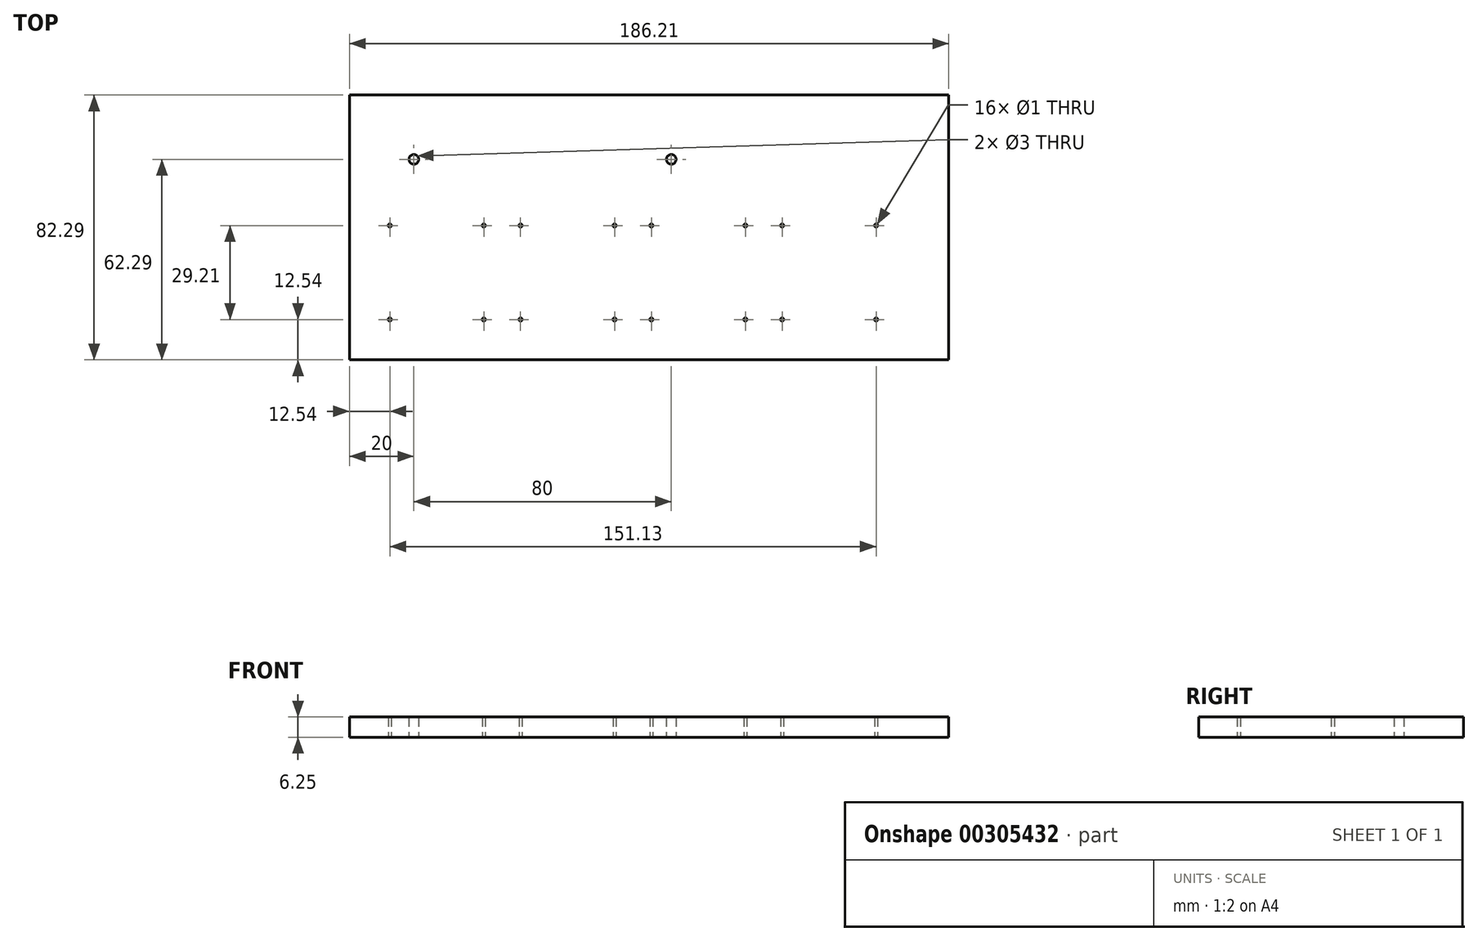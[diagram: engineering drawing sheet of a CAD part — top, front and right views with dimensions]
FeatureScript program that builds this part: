
annotation { "Feature Type Name" : "Feature", "Feature Type Description" : "" }
export const myFeature = defineFeature(function(context is Context, id is Id, definition is map)
    precondition{}
    {
        {
            var Q0;
            Q0=qCreatedBy(makeId("Top.planeOp"),FACE);
            var sketch = newSketch(context, id + "F0", { "sketchPlane" : qUnion([Q0])});
            skLineSegment(sketch, "E0.bottom", {"start": v(0, 0) * mm, "end": v(34.3, 0) * mm, "construction": true});
            skLineSegment(sketch, "E0.top", {"start": v(0, 34.3) * mm, "end": v(34.3, 34.3) * mm, "construction": true});
            skLineSegment(sketch, "E0.left", {"start": v(0, 0) * mm, "end": v(0, 34.3) * mm, "construction": true});
            skLineSegment(sketch, "E0.right", {"start": v(34.29, 0) * mm, "end": v(34.29, 34.3) * mm, "construction": true});
            skLineSegment(sketch, "E1.bottom", {"start": v(2.54, 31.75) * mm, "end": v(31.75, 31.75) * mm, "construction": true});
            skLineSegment(sketch, "E1.top", {"start": v(2.54, 2.54) * mm, "end": v(31.75, 2.54) * mm, "construction": true});
            skLineSegment(sketch, "E1.left", {"start": v(2.54, 31.75) * mm, "end": v(2.54, 2.54) * mm, "construction": true});
            skLineSegment(sketch, "E1.right", {"start": v(31.75, 31.75) * mm, "end": v(31.75, 2.54) * mm, "construction": true});
            skPoint(sketch, "E2", {"position": v(17.15, 31.75) * mm});
            skPoint(sketch, "E3", {"position": v(17.15, 34.3) * mm});
            skPoint(sketch, "E4", {"position": v(34.29, 17.15) * mm});
            skPoint(sketch, "E5", {"position": v(31.75, 17.15) * mm});
            skLineSegment(sketch, "E6.1.0.0", {"start": v(40.64, 0) * mm, "end": v(40.64, 34.3) * mm, "construction": true});
            skPoint(sketch, "E6.1.0.1", {"position": v(72.39, 17.15) * mm});
            skLineSegment(sketch, "E6.1.0.2", {"start": v(74.93, 0) * mm, "end": v(74.93, 34.3) * mm, "construction": true});
            skPoint(sketch, "E6.1.0.3", {"position": v(74.93, 17.15) * mm});
            skLineSegment(sketch, "E6.1.0.4", {"start": v(43.18, 31.75) * mm, "end": v(72.39, 31.75) * mm, "construction": true});
            skPoint(sketch, "E6.1.0.5", {"position": v(57.78, 34.3) * mm});
            skLineSegment(sketch, "E6.1.0.6", {"start": v(43.18, 2.54) * mm, "end": v(72.39, 2.54) * mm, "construction": true});
            skLineSegment(sketch, "E6.1.0.7", {"start": v(40.64, 34.3) * mm, "end": v(74.93, 34.3) * mm, "construction": true});
            skLineSegment(sketch, "E6.1.0.8", {"start": v(43.18, 31.75) * mm, "end": v(43.18, 2.54) * mm, "construction": true});
            skPoint(sketch, "E6.1.0.9", {"position": v(57.78, 31.75) * mm});
            skLineSegment(sketch, "E6.1.0.10", {"start": v(72.39, 31.75) * mm, "end": v(72.39, 2.54) * mm, "construction": true});
            skLineSegment(sketch, "E6.1.0.11", {"start": v(40.64, 0) * mm, "end": v(74.93, 0) * mm, "construction": true});
            skLineSegment(sketch, "E6.2.0.0", {"start": v(81.28, 0) * mm, "end": v(81.28, 34.3) * mm, "construction": true});
            skPoint(sketch, "E6.2.0.1", {"position": v(113.03, 17.15) * mm});
            skLineSegment(sketch, "E6.2.0.2", {"start": v(115.57, 0) * mm, "end": v(115.57, 34.3) * mm, "construction": true});
            skPoint(sketch, "E6.2.0.3", {"position": v(115.57, 17.15) * mm});
            skLineSegment(sketch, "E6.2.0.4", {"start": v(83.82, 31.75) * mm, "end": v(113.03, 31.75) * mm, "construction": true});
            skPoint(sketch, "E6.2.0.5", {"position": v(98.42, 34.3) * mm});
            skLineSegment(sketch, "E6.2.0.6", {"start": v(83.82, 2.54) * mm, "end": v(113.03, 2.54) * mm, "construction": true});
            skLineSegment(sketch, "E6.2.0.7", {"start": v(81.28, 34.3) * mm, "end": v(115.57, 34.3) * mm, "construction": true});
            skLineSegment(sketch, "E6.2.0.8", {"start": v(83.82, 31.75) * mm, "end": v(83.82, 2.54) * mm, "construction": true});
            skPoint(sketch, "E6.2.0.9", {"position": v(98.42, 31.75) * mm});
            skLineSegment(sketch, "E6.2.0.10", {"start": v(113.03, 31.75) * mm, "end": v(113.03, 2.54) * mm, "construction": true});
            skLineSegment(sketch, "E6.2.0.11", {"start": v(81.28, 0) * mm, "end": v(115.57, 0) * mm, "construction": true});
            skLineSegment(sketch, "E6.3.0.0", {"start": v(121.92, 0) * mm, "end": v(121.92, 34.3) * mm, "construction": true});
            skPoint(sketch, "E6.3.0.1", {"position": v(153.67, 17.15) * mm});
            skLineSegment(sketch, "E6.3.0.2", {"start": v(156.2, 0) * mm, "end": v(156.2, 34.3) * mm, "construction": true});
            skPoint(sketch, "E6.3.0.3", {"position": v(156.2, 17.15) * mm});
            skLineSegment(sketch, "E6.3.0.4", {"start": v(124.46, 31.75) * mm, "end": v(153.67, 31.75) * mm, "construction": true});
            skPoint(sketch, "E6.3.0.5", {"position": v(139.06, 34.3) * mm});
            skLineSegment(sketch, "E6.3.0.6", {"start": v(124.46, 2.54) * mm, "end": v(153.67, 2.54) * mm, "construction": true});
            skLineSegment(sketch, "E6.3.0.7", {"start": v(121.92, 34.3) * mm, "end": v(156.2, 34.3) * mm, "construction": true});
            skLineSegment(sketch, "E6.3.0.8", {"start": v(124.46, 31.75) * mm, "end": v(124.46, 2.54) * mm, "construction": true});
            skPoint(sketch, "E6.3.0.9", {"position": v(139.06, 31.75) * mm});
            skLineSegment(sketch, "E6.3.0.10", {"start": v(153.67, 31.75) * mm, "end": v(153.67, 2.54) * mm, "construction": true});
            skLineSegment(sketch, "E6.3.0.11", {"start": v(121.92, 0) * mm, "end": v(156.2, 0) * mm, "construction": true});
            skLineSegment(sketch, "E6.direction1", {"start": v(0, 0) * mm, "end": v(40.64, 0) * mm, "construction": true});
            skLineSegment(sketch, "E7.bottom", {"start": v(0, 62.3) * mm, "end": v(100, 62.3) * mm, "construction": true});
            skLineSegment(sketch, "E7.top", {"start": v(0, 42.3) * mm, "end": v(100, 42.29) * mm, "construction": true});
            skLineSegment(sketch, "E7.left", {"start": v(0, 62.29) * mm, "end": v(0, 42.3) * mm, "construction": true});
            skLineSegment(sketch, "E7.right", {"start": v(100, 62.29) * mm, "end": v(100, 42.3) * mm, "construction": true});
            skPoint(sketch, "E8", {"position": v(0, 52.29) * mm});
            skPoint(sketch, "E9", {"position": v(10, 52.29) * mm});
            skPoint(sketch, "E10", {"position": v(90, 52.3) * mm});
            skPoint(sketch, "E11", {"position": v(50, 62.3) * mm});
            skPoint(sketch, "E12", {"position": v(50, 52.29) * mm});
            skPoint(sketch, "E13.endSnap0", {"position": v(50, 42.3) * mm});
            skLineSegment(sketch, "E14.bottom", {"start": v(-10, -10) * mm, "end": v(176.2, -10) * mm});
            skLineSegment(sketch, "E14.top", {"start": v(-10, 72.29) * mm, "end": v(176.2, 72.29) * mm});
            skLineSegment(sketch, "E14.left", {"start": v(-10, -10) * mm, "end": v(-10, 72.29) * mm});
            skLineSegment(sketch, "E14.right", {"start": v(176.2, -10) * mm, "end": v(176.2, 72.29) * mm});
            skSolve(sketch);
        }
        {
            var Q0;
            Q0=makeQuery(id+"F0.imprint","IMPRINT",FACE,{"disambiguationData":[TD([[makeQuery(id+"F0.imprint","IMPRINT",EDGE,{"derivedFrom":sQuery(id+"F0.wireOp",EDGE,"E14.bottom")}),1.0]])]});
            extrude(context, id + "F1", {"entities" : qUnion([Q0]), "depth" : 6.25 * mm});
        }
        {
            var Q0;
            Q0=sQuery(id+"F0.wireOp",VERTEX,"E1.top.start");
            var Q1;
            Q1=sQuery(id+"F0.wireOp",VERTEX,"E1.left.start");
            var Q2;
            Q2=sQuery(id+"F0.wireOp",VERTEX,"E1.bottom.end");
            var Q3;
            Q3=sQuery(id+"F0.wireOp",VERTEX,"E1.top.end");
            var Q4;
            Q4=sQuery(id+"F0.wireOp",VERTEX,"E6.1.0.6.start");
            var Q5;
            Q5=sQuery(id+"F0.wireOp",VERTEX,"E6.1.0.4.start");
            var Q6;
            Q6=sQuery(id+"F0.wireOp",VERTEX,"E6.1.0.10.start");
            var Q7;
            Q7=sQuery(id+"F0.wireOp",VERTEX,"E6.1.0.6.end");
            var Q8;
            Q8=sQuery(id+"F0.wireOp",VERTEX,"E6.2.0.6.start");
            var Q9;
            Q9=sQuery(id+"F0.wireOp",VERTEX,"E6.2.0.4.start");
            var Q10;
            Q10=sQuery(id+"F0.wireOp",VERTEX,"E6.2.0.10.start");
            var Q11;
            Q11=sQuery(id+"F0.wireOp",VERTEX,"E6.2.0.6.end");
            var Q12;
            Q12=sQuery(id+"F0.wireOp",VERTEX,"E6.3.0.6.start");
            var Q13;
            Q13=sQuery(id+"F0.wireOp",VERTEX,"E6.3.0.4.start");
            var Q14;
            Q14=sQuery(id+"F0.wireOp",VERTEX,"E6.3.0.10.start");
            var Q15;
            Q15=sQuery(id+"F0.wireOp",VERTEX,"E6.3.0.6.end");
            var Q16;
            Q16=makeQuery(id+"F1.opExtrude","SWEPT_BODY",BODY,{"disambiguationData":[OSD([sQuery(id+"F0.wireOp",EDGE,"E14.bottom"),sQuery(id+"F0.wireOp",EDGE,"E14.top"),sQuery(id+"F0.wireOp",EDGE,"E14.left"),sQuery(id+"F0.wireOp",EDGE,"E14.right")])]});
            hole(context, id + "F2", {"style" : HoleStyle.SIMPLE, "endStyle" : HoleEndStyle.THROUGH, "oppositeDirection" : true, "holeDiameter" : 1 * mm, "isTappedThrough" : true, "tappedDepth" : 12 * mm, "tapClearance" : 3, "startFromSketch" : true, "locations" : qUnion([Q0, Q1, Q2, Q3, Q4, Q5, Q6, Q7, Q8, Q9, Q10, Q11, Q12, Q13, Q14, Q15]), "scope" : qUnion([Q16])});
        }
        {
            var Q0;
            Q0=sQuery(id+"F0.wireOp",VERTEX,"E9");
            var Q1;
            Q1=sQuery(id+"F0.wireOp",VERTEX,"E10");
            var Q2;
            Q2=makeQuery(id+"F1.opExtrude","SWEPT_BODY",BODY,{"disambiguationData":[OSD([sQuery(id+"F0.wireOp",EDGE,"E14.bottom"),sQuery(id+"F0.wireOp",EDGE,"E14.top"),sQuery(id+"F0.wireOp",EDGE,"E14.left"),sQuery(id+"F0.wireOp",EDGE,"E14.right")])]});
            hole(context, id + "F3", {"style" : HoleStyle.SIMPLE, "endStyle" : HoleEndStyle.THROUGH, "oppositeDirection" : true, "holeDiameter" : 3 * mm, "isTappedThrough" : true, "tappedDepth" : 12 * mm, "tapClearance" : 3, "startFromSketch" : true, "locations" : qUnion([Q0, Q1]), "scope" : qUnion([Q2])});
        }
    });
